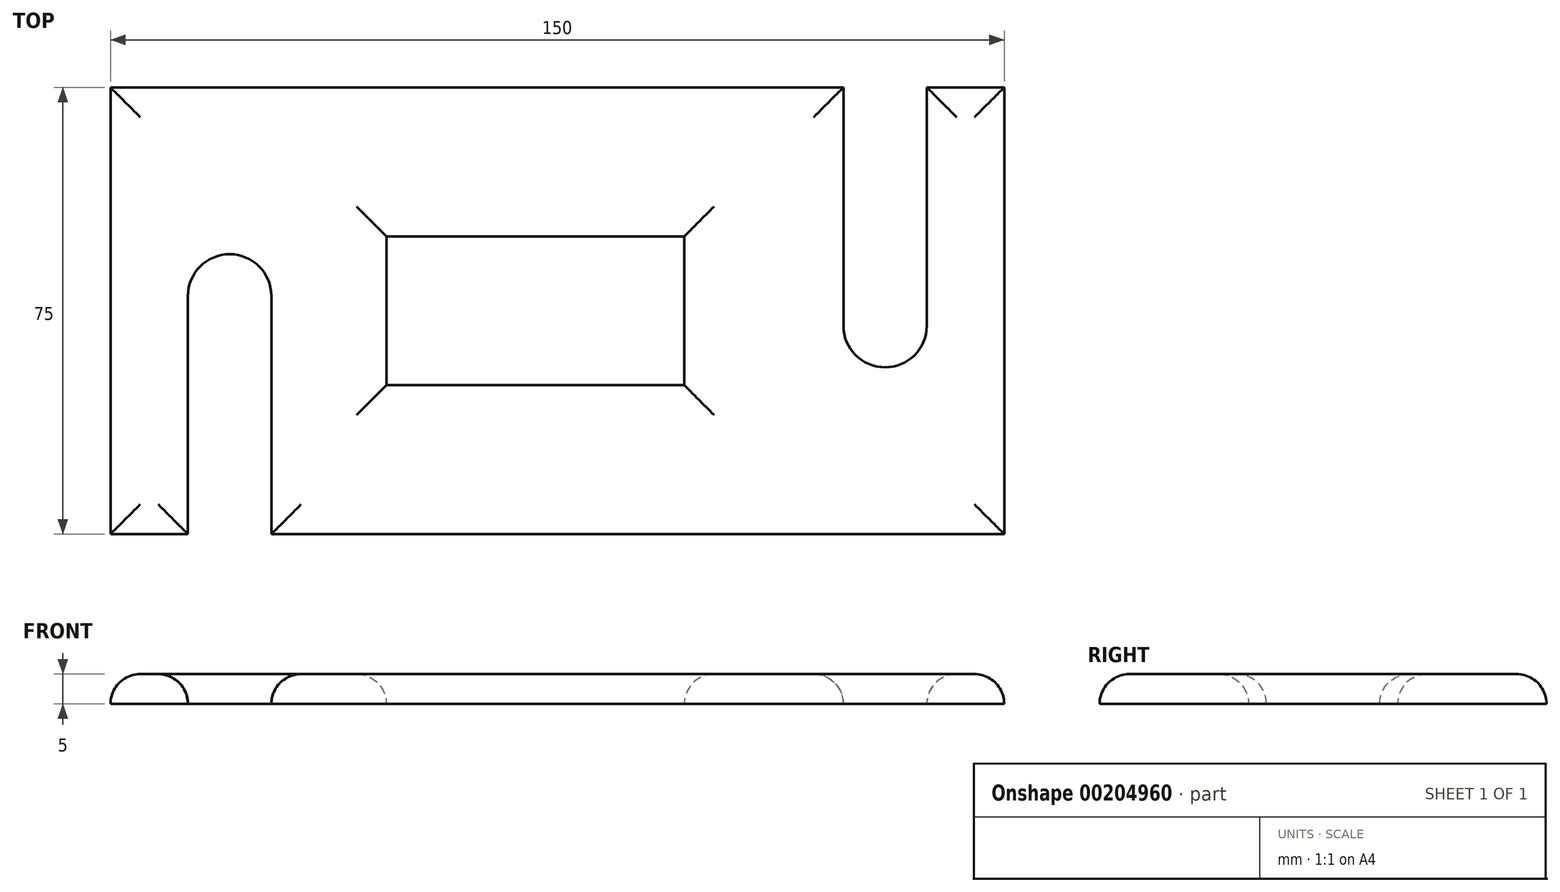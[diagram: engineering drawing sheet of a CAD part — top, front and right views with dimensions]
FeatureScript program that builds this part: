
annotation { "Feature Type Name" : "Feature", "Feature Type Description" : "" }
export const myFeature = defineFeature(function(context is Context, id is Id, definition is map)
    precondition{}
    {
        {
            var Q0;
            Q0=qCreatedBy(makeId("Top.planeOp"),FACE);
            var sketch = newSketch(context, id + "F0", { "sketchPlane" : qUnion([Q0])});
            skLineSegment(sketch, "E0.bottom", {"start": v(0, 75) * mm, "end": v(150, 75) * mm});
            skLineSegment(sketch, "E0.top", {"start": v(0, 0) * mm, "end": v(150, 0) * mm});
            skLineSegment(sketch, "E0.left", {"start": v(0, 75) * mm, "end": v(0, 0) * mm});
            skLineSegment(sketch, "E0.right", {"start": v(150, 75) * mm, "end": v(150, 0) * mm});
            skSolve(sketch);
        }
        {
            var Q0;
            Q0 = qSketchRegion(id + "F0", true);
            extrude(context, id + "F1", {"entities" : qUnion([Q0]), "depth" : 5 * mm});
        }
        {
            var Q0;
            Q0=makeQuery(id+"F1.opExtrude","CAP_FACE",FACE,{"disambiguationData":[OSD([sQuery(id+"F0.wireOp",EDGE,"E0.bottom"),sQuery(id+"F0.wireOp",EDGE,"E0.top"),sQuery(id+"F0.wireOp",EDGE,"E0.left"),sQuery(id+"F0.wireOp",EDGE,"E0.right")])],"isStart":false});
            var sketch = newSketch(context, id + "F2", { "sketchPlane" : qUnion([Q0])});
            skLineSegment(sketch, "E1", {"start": v(13, 0) * mm, "end": v(13, 40) * mm});
            skArc(sketch, "E2", {"start": v(27, 40) * mm, "mid": v(20, 47) * mm, "end": v(13, 40) * mm});
            skLineSegment(sketch, "E3", {"start": v(27, 40) * mm, "end": v(27, 0) * mm});
            skSolve(sketch);
        }
        {
            var Q0;
            Q0 = qSketchRegion(id + "F2", true);
            var Q1;
            {var subQ0=sQuery(id+"F2.wireOp",EDGE,"E1");Q1=makeQuery(id+"F2.imprint","IMPRINT",FACE,{"disambiguationData":[TD([[makeQuery(id+"F2.imprint","IMPRINT",EDGE,{"derivedFrom":subQ0}),-1.0]])]});}
            extrude(context, id + "F3", {"entities" : qUnion([Q0, Q1]), "operationType" : NewBodyOperationType.REMOVE, "endBound" : BoundingType.THROUGH_ALL, "oppositeDirection" : true, "depth" : 25 * mm});
        }
        {
            var Q0;
            Q0=makeQuery(id+"F1.opExtrude","CAP_FACE",FACE,{"disambiguationData":[OSD([sQuery(id+"F0.wireOp",EDGE,"E0.bottom"),sQuery(id+"F0.wireOp",EDGE,"E0.top"),sQuery(id+"F0.wireOp",EDGE,"E0.left"),sQuery(id+"F0.wireOp",EDGE,"E0.right")])],"isStart":false});
            var sketch = newSketch(context, id + "F4", { "sketchPlane" : qUnion([Q0])});
            skLineSegment(sketch, "E4", {"start": v(137, 75) * mm, "end": v(137, 35) * mm});
            skArc(sketch, "E5", {"start": v(123, 35) * mm, "mid": v(130, 28) * mm, "end": v(137, 35) * mm});
            skLineSegment(sketch, "E6", {"start": v(123, 35) * mm, "end": v(123, 75) * mm});
            skSolve(sketch);
        }
        {
            var Q0;
            Q0 = qSketchRegion(id + "F4", true);
            var Q1;
            {var subQ0=sQuery(id+"F4.wireOp",EDGE,"E4");Q1=makeQuery(id+"F4.imprint","IMPRINT",FACE,{"disambiguationData":[TD([[makeQuery(id+"F4.imprint","IMPRINT",EDGE,{"derivedFrom":subQ0}),-1.0]])]});}
            extrude(context, id + "F5", {"entities" : qUnion([Q0, Q1]), "operationType" : NewBodyOperationType.REMOVE, "endBound" : BoundingType.THROUGH_ALL, "oppositeDirection" : true, "depth" : 25 * mm});
        }
        {
            var Q0;
            Q0=makeQuery(id+"F1.opExtrude","CAP_FACE",FACE,{"disambiguationData":[OSD([sQuery(id+"F0.wireOp",EDGE,"E0.bottom"),sQuery(id+"F0.wireOp",EDGE,"E0.top"),sQuery(id+"F0.wireOp",EDGE,"E0.left"),sQuery(id+"F0.wireOp",EDGE,"E0.right")])],"isStart":false});
            var sketch = newSketch(context, id + "F6", { "sketchPlane" : qUnion([Q0])});
            skLineSegment(sketch, "E7", {"start": v(46.3, 50) * mm, "end": v(96.3, 50) * mm});
            skLineSegment(sketch, "E8", {"start": v(96.3, 50) * mm, "end": v(96.3, 25) * mm});
            skLineSegment(sketch, "E9", {"start": v(96.3, 25) * mm, "end": v(46.3, 25) * mm});
            skLineSegment(sketch, "E10", {"start": v(46.3, 25) * mm, "end": v(46.3, 50) * mm});
            skSolve(sketch);
        }
        {
            var Q0;
            Q0=makeQuery(id+"F6.imprint","IMPRINT",FACE,{"disambiguationData":[TD([[makeQuery(id+"F6.imprint","IMPRINT",EDGE,{"derivedFrom":sQuery(id+"F6.wireOp",EDGE,"E7")}),-1.0]])]});
            extrude(context, id + "F7", {"entities" : qUnion([Q0]), "operationType" : NewBodyOperationType.REMOVE, "endBound" : BoundingType.THROUGH_ALL, "oppositeDirection" : true, "depth" : 25 * mm});
        }
        {
            var Q0;
            Q0=makeQuery(id+"F1.opExtrude","CAP_FACE",FACE,{"disambiguationData":[OSD([sQuery(id+"F0.wireOp",EDGE,"E0.bottom"),sQuery(id+"F0.wireOp",EDGE,"E0.top"),sQuery(id+"F0.wireOp",EDGE,"E0.left"),sQuery(id+"F0.wireOp",EDGE,"E0.right")])],"isStart":false});
            fillet(context, id + "F8", {"entities" : qUnion([Q0]), "radius" : 5 * mm, "tangentPropagation" : true, "allowEdgeOverflow" : false});
        }
    });
